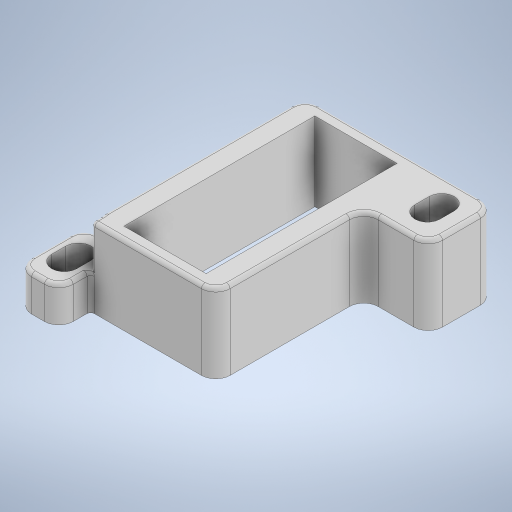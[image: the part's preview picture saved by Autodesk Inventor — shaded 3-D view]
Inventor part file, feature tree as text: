
AUTODESK INVENTOR PART (.ipt)
format: ipt  version: 2023.1 (Build 271208000, 208)  size: 348,160 bytes
history: native  units: mm
features: fillet x5, extrude x3, sketch x2
ambient origin geometry x8: Origin, YZ Plane, XZ Plane, XY Plane, X Axis, Y Axis, Z Axis, Center Point
bodies: Solid1 (feature_tree)
feature tree (10):
  sketch  "Sketch1"  dims[d0=11.5mm d1=26.7mm]
  extrude  "Extrusion1"  Depth=26.7mm
  extrude  "Extrusion2"  Depth=0.5mm
  extrude  "Extrusion3"  Depth=0.5mm
  fillet  "Fillet1"  Radius=1.65mm
  fillet  "Fillet2"  Radius=8.0mm
  fillet  "Fillet3"  Radius=2.0mm
  fillet  "Fillet4"  Radius=3.5mm
  fillet  "Fillet5"  Radius=9.0mm
  sketch  "Sketch2"  dims[d2=17.5mm d3=30.0mm d4=3.0mm d5=1.65mm d6=8.0mm d7=2.0mm d8=3.5mm d9=9.0mm d10=9.3mm d11=11.0mm d12=0.0mm d13=25.4mm d14=25.4mm d15=2.0mm d16=3.5mm d17=9.3mm d18=5.8mm d19=1.9mm d20=1.9mm d21=5.0mm d22=0.0mm d23=1.25mm d24=5.0mm d25=0.0mm d26=2.0mm d27=0.5mm d28=0.5mm d29=0.5mm d30=0.5mm]
